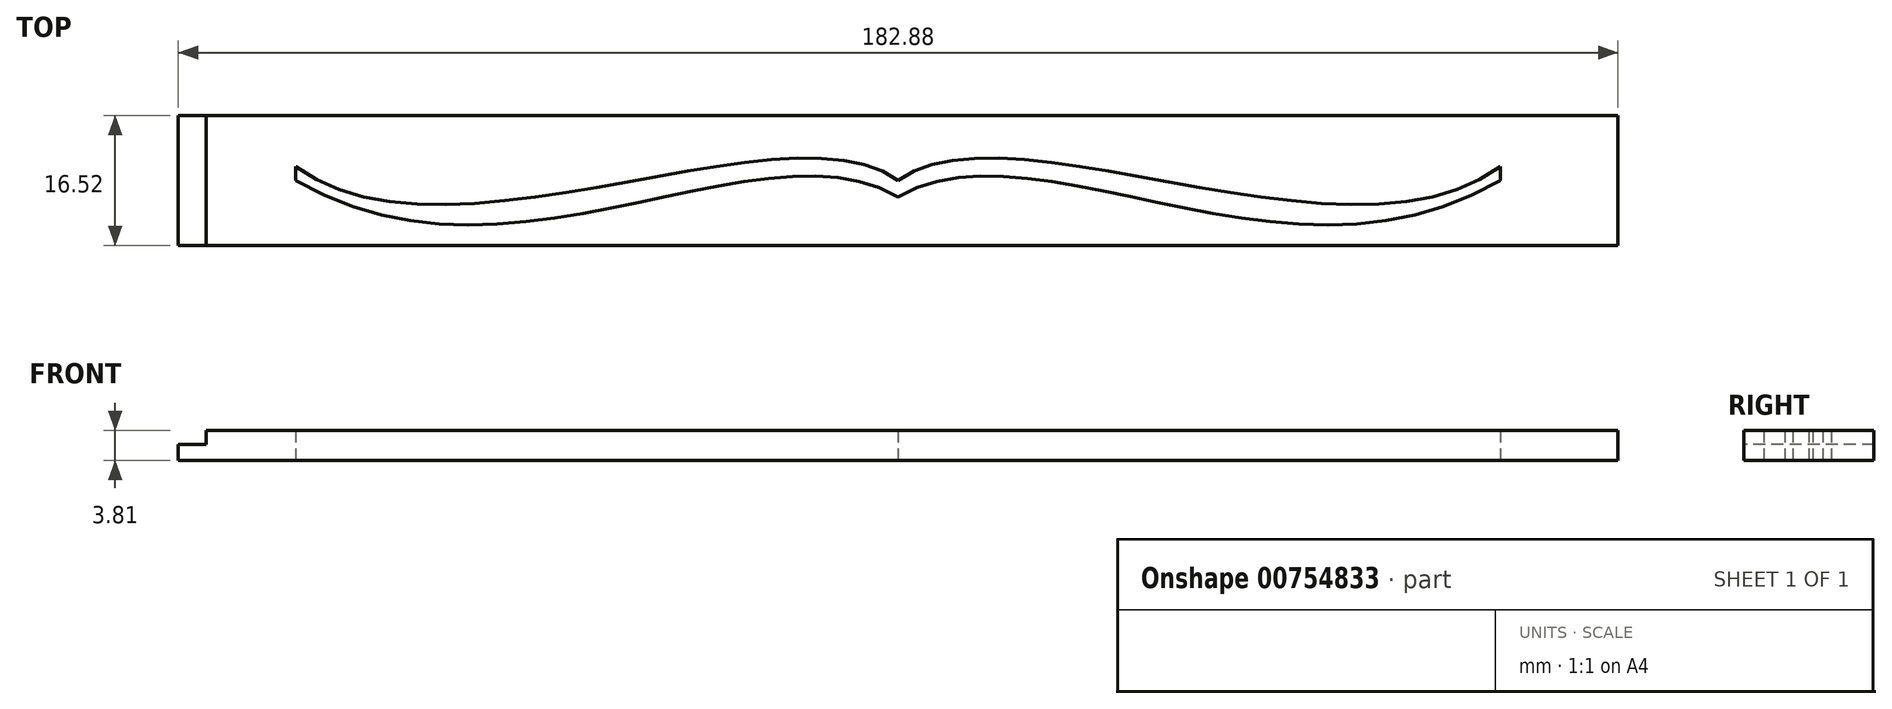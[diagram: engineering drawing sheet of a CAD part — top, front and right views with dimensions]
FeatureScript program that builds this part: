
annotation { "Feature Type Name" : "Feature", "Feature Type Description" : "" }
export const myFeature = defineFeature(function(context is Context, id is Id, definition is map)
    precondition{}
    {
        {
            var Q0;
            Q0=qCreatedBy(makeId("Top.planeOp"),FACE);
            var sketch = newSketch(context, id + "F0", { "sketchPlane" : qUnion([Q0])});
            skLineSegment(sketch, "E0.bottom", {"start": v(-91.44, 8.26) * mm, "end": v(91.44, 8.26) * mm});
            skLineSegment(sketch, "E0.top", {"start": v(-91.44, -8.25) * mm, "end": v(91.44, -8.25) * mm});
            skLineSegment(sketch, "E0.left", {"start": v(-91.44, 8.26) * mm, "end": v(-91.44, -8.25) * mm});
            skLineSegment(sketch, "E0.right", {"start": v(91.44, 8.26) * mm, "end": v(91.44, -8.25) * mm});
            skPoint(sketch, "E0.middle", {"position": v(0, 0) * mm});
            skFitSpline(sketch, "E1", {"points": [v(0, -2.07) * mm, v(-76.5, 0) * mm], "startDerivative": vector(-53.73, 30.99) * mm, "endDerivative": vector(-82.17, 48.06) * mm});
            skFitSpline(sketch, "E2", {"points": [v(-76.5, 1.74) * mm, v(0, 0) * mm], "startDerivative": vector(57.81, -42.7) * mm, "endDerivative": vector(42.47, -31.5) * mm});
            skLineSegment(sketch, "E3", {"start": v(-76.5, 1.74) * mm, "end": v(-76.5, 0) * mm});
            skFitSpline(sketch, "E4.MirrorCS", {"points": [v(0, -2.07) * mm, v(76.5, 0) * mm], "startDerivative": vector(53.73, 30.99) * mm, "endDerivative": vector(82.17, 48.06) * mm});
            skFitSpline(sketch, "E5.MirrorCS", {"points": [v(76.5, 1.74) * mm, v(0, 0) * mm], "startDerivative": vector(-57.81, -42.7) * mm, "endDerivative": vector(-42.47, -31.5) * mm});
            skLineSegment(sketch, "E6.MirrorCS", {"start": v(76.5, 1.74) * mm, "end": v(76.5, 0) * mm});
            skSolve(sketch);
        }
        {
            var Q0;
            Q0=makeQuery(id+"F0.imprint","IMPRINT",FACE,{"disambiguationData":[TD([[makeQuery(id+"F0.imprint","IMPRINT",EDGE,{"derivedFrom":sQuery(id+"F0.wireOp",EDGE,"E0.bottom")}),-1.0]])]});
            extrude(context, id + "F1", {"entities" : qUnion([Q0]), "depth" : 3.8 * mm, "offsetDistance" : 25.4 * mm});
        }
        {
            var Q0;
            Q0=makeQuery(id+"F1.opExtrude","CAP_FACE",FACE,{"disambiguationData":[OSD([sQuery(id+"F0.wireOp",EDGE,"E0.bottom"),sQuery(id+"F0.wireOp",EDGE,"E0.top"),sQuery(id+"F0.wireOp",EDGE,"E0.left"),sQuery(id+"F0.wireOp",EDGE,"E0.right"),sQuery(id+"F0.wireOp",EDGE,"E1"),sQuery(id+"F0.wireOp",EDGE,"E2"),sQuery(id+"F0.wireOp",EDGE,"E3"),sQuery(id+"F0.wireOp",EDGE,"E4.MirrorCS"),sQuery(id+"F0.wireOp",EDGE,"E5.MirrorCS"),sQuery(id+"F0.wireOp",EDGE,"E6.MirrorCS")])],"isStart":false});
            var sketch = newSketch(context, id + "F2", { "sketchPlane" : qUnion([Q0])});
            skLineSegment(sketch, "E7", {"start": v(-87.88, 8.26) * mm, "end": v(-87.88, -8.25) * mm});
            skLineSegment(sketch, "E8.MirrorCS", {"start": v(87.88, 8.26) * mm, "end": v(87.88, -8.25) * mm});
            skSolve(sketch);
        }
        {
            var Q0;
            {var subQ0=sQuery(id+"F2.wireOp",EDGE,"E7");Q0=makeQuery(id+"F2.imprint","IMPRINT",FACE,{"disambiguationData":[TD([[makeQuery(id+"F2.imprint","IMPRINT",EDGE,{"derivedFrom":subQ0}),-1.0]])]});}
            extrude(context, id + "F3", {"entities" : qUnion([Q0]), "operationType" : NewBodyOperationType.REMOVE, "oppositeDirection" : true, "depth" : 1.78 * mm, "offsetDistance" : 25.4 * mm});
        }
    });
